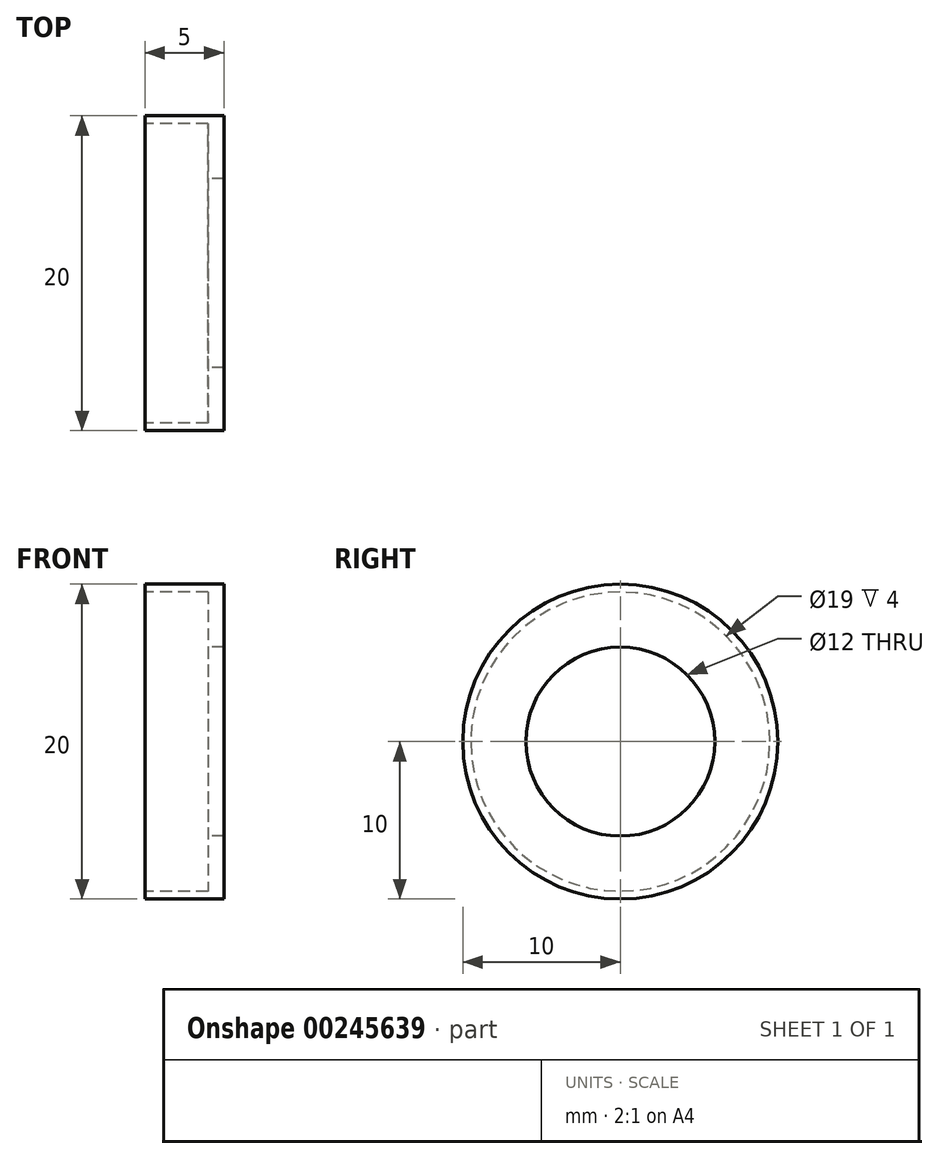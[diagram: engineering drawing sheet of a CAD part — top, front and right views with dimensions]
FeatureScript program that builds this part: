
annotation { "Feature Type Name" : "Feature", "Feature Type Description" : "" }
export const myFeature = defineFeature(function(context is Context, id is Id, definition is map)
    precondition{}
    {
        {
            var Q0;
            Q0=qCreatedBy(makeId("Right.planeOp"),FACE);
            var sketch = newSketch(context, id + "F0", { "sketchPlane" : qUnion([Q0])});
            skCircle(sketch, "E0", {"center": v(0, 0) * mm, "radius": 10 * mm});
            skSolve(sketch);
        }
        {
            var Q0;
            Q0=makeQuery(id+"F0.imprint","IMPRINT",FACE,{"disambiguationData":[TD([[makeQuery(id+"F0.imprint","IMPRINT",EDGE,{"derivedFrom":sQuery(id+"F0.wireOp",EDGE,"E0")}),1.0]])]});
            extrude(context, id + "F1", {"entities" : qUnion([Q0]), "depth" : 5 * mm});
        }
        {
            var Q0;
            Q0=makeQuery(id+"F1.opExtrude","CAP_FACE",FACE,{"disambiguationData":[OSD([sQuery(id+"F0.wireOp",EDGE,"E0")])],"isStart":true});
            var sketch = newSketch(context, id + "F2", { "sketchPlane" : qUnion([Q0])});
            skCircle(sketch, "E1", {"center": v(0, 0) * mm, "radius": 9.5 * mm});
            skSolve(sketch);
        }
        {
            var Q0;
            Q0=makeQuery(id+"F2.imprint","IMPRINT",FACE,{"disambiguationData":[TD([[makeQuery(id+"F2.imprint","IMPRINT",EDGE,{"derivedFrom":sQuery(id+"F2.wireOp",EDGE,"E1")}),1.0]])]});
            extrude(context, id + "F3", {"entities" : qUnion([Q0]), "operationType" : NewBodyOperationType.REMOVE, "oppositeDirection" : true, "depth" : 4 * mm});
        }
        {
            var Q0;
            Q0=makeQuery(id+"F1.opExtrude","CAP_FACE",FACE,{"disambiguationData":[OSD([sQuery(id+"F0.wireOp",EDGE,"E0")])],"isStart":false});
            var sketch = newSketch(context, id + "F4", { "sketchPlane" : qUnion([Q0])});
            skPoint(sketch, "E2", {"position": v(0, 0) * mm});
            skSolve(sketch);
        }
        {
            var Q0;
            Q0=sQuery(id+"F4.wireOp",VERTEX,"E2");
            var Q1;
            Q1=makeQuery(id+"F1.opExtrude","SWEPT_BODY",BODY,{"disambiguationData":[OSD([sQuery(id+"F0.wireOp",EDGE,"E0")])]});
            hole(context, id + "F5", {"style" : HoleStyle.SIMPLE, "endStyle" : HoleEndStyle.THROUGH, "holeDiameter" : 12 * mm, "tappedDepth" : 15 * mm, "tapClearance" : 0, "locations" : qUnion([Q0]), "scope" : qUnion([Q1]), "startStyle" : HoleStartStyle.SKETCH});
        }
    });
